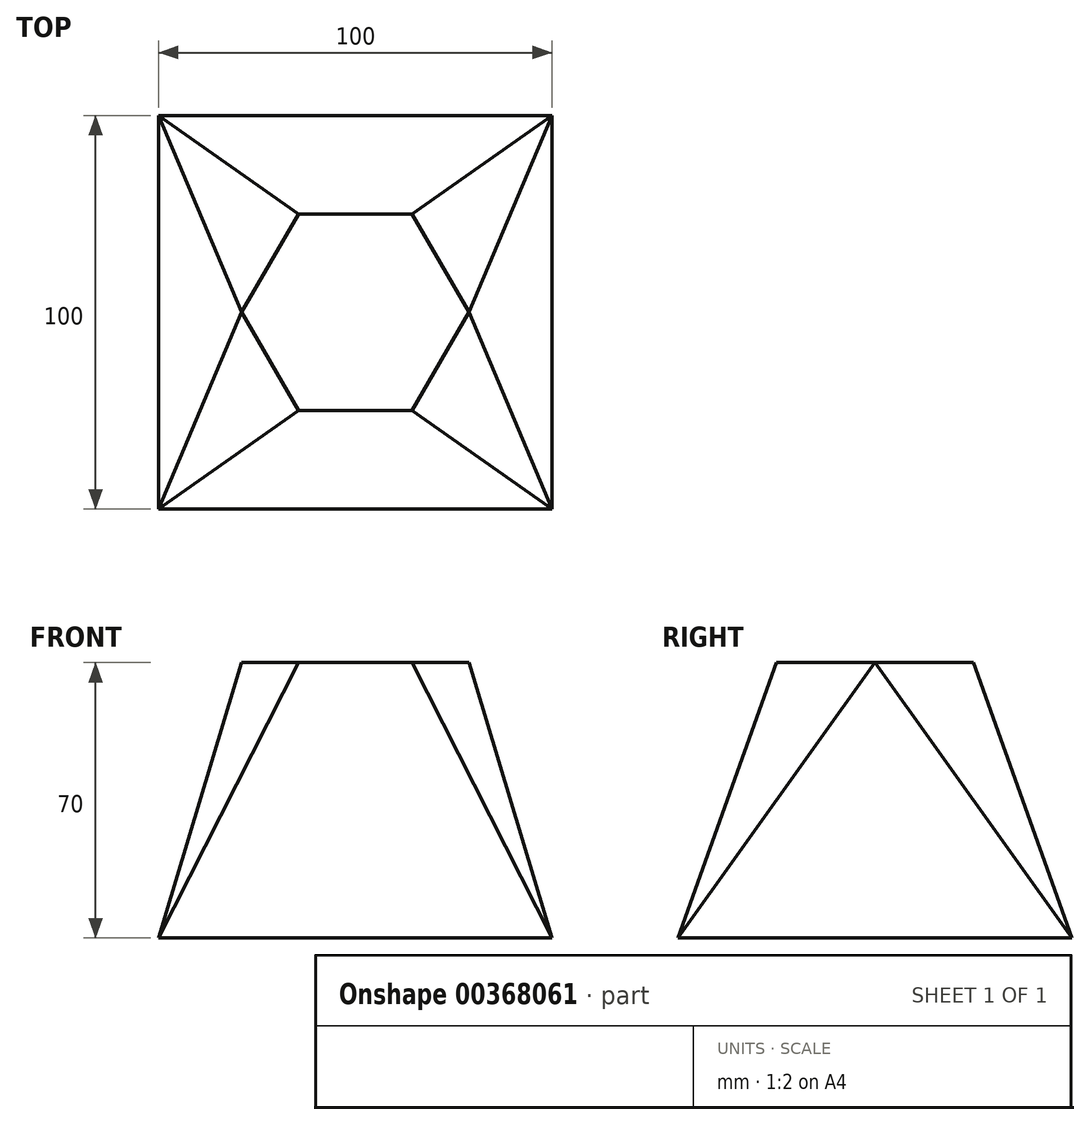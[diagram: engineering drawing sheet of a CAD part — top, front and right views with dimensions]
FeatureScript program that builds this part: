
annotation { "Feature Type Name" : "Feature", "Feature Type Description" : "" }
export const myFeature = defineFeature(function(context is Context, id is Id, definition is map)
    precondition{}
    {
        {
            var Q0;
            Q0=qCreatedBy(makeId("Top.planeOp"),FACE);
            var sketch = newSketch(context, id + "F0", { "sketchPlane" : qUnion([Q0])});
            skLineSegment(sketch, "E0.bottom", {"start": v(50, -50) * mm, "end": v(-50, -50) * mm});
            skLineSegment(sketch, "E0.top", {"start": v(50, 50) * mm, "end": v(-50, 50) * mm});
            skLineSegment(sketch, "E0.left", {"start": v(50, -50) * mm, "end": v(50, 50) * mm});
            skLineSegment(sketch, "E0.right", {"start": v(-50, -50) * mm, "end": v(-50, 50) * mm});
            skPoint(sketch, "E0.middle", {"position": v(0, 0) * mm});
            skSolve(sketch);
        }
        {
            var Q0;
            Q0=qCreatedBy(makeId("Top.planeOp"),FACE);
            cPlane(context, id + "F1", {"entities" : qUnion([Q0]), "cplaneType" : CPlaneType.OFFSET, "offset" : 70 * mm, "width" : 150 * mm, "height" : 150 * mm});
        }
        {
            var Q0;
            Q0=qCreatedBy(id+"F1.planeOp",FACE);
            var sketch = newSketch(context, id + "F2", { "sketchPlane" : qUnion([Q0])});
            skCircle(sketch, "E1.cCircle", {"center": v(0, 0) * mm, "radius": 25 * mm, "construction": true});
            skLineSegment(sketch, "E1.0", {"start": v(-14.43, 25) * mm, "end": v(14.43, 25) * mm});
            skLineSegment(sketch, "E1.1", {"start": v(14.43, 25) * mm, "end": v(28.87, 0) * mm});
            skLineSegment(sketch, "E1.2", {"start": v(28.87, 0) * mm, "end": v(14.43, -25) * mm});
            skLineSegment(sketch, "E1.3", {"start": v(14.43, -25) * mm, "end": v(-14.43, -25) * mm});
            skLineSegment(sketch, "E1.4", {"start": v(-14.43, -25) * mm, "end": v(-28.87, 0) * mm});
            skLineSegment(sketch, "E1.5", {"start": v(-28.87, 0) * mm, "end": v(-14.43, 25) * mm});
            skPoint(sketch, "E1.0.midPoint", {"position": v(0, 25) * mm});
            skLineSegment(sketch, "E2", {"start": v(-14.43, 25) * mm, "end": v(-14.43, -25) * mm});
            skLineSegment(sketch, "E3", {"start": v(14.43, 25) * mm, "end": v(14.43, -25) * mm});
            skSolve(sketch);
        }
        {
            var Q0;
            Q0=makeQuery(id+"F2.imprint","IMPRINT",FACE,{"disambiguationData":[TD([[makeQuery(id+"F2.imprint","IMPRINT",EDGE,{"derivedFrom":sQuery(id+"F2.wireOp",EDGE,"E1.0")}),-1.0]])]});
            var Q1;
            Q1=makeQuery(id+"F0.imprint","IMPRINT",FACE,{"disambiguationData":[TD([[makeQuery(id+"F0.imprint","IMPRINT",EDGE,{"derivedFrom":sQuery(id+"F0.wireOp",EDGE,"E0.bottom")}),-1.0]])]});
            loft(context, id + "F3", {"sheetProfilesArray" : [{ "sheetProfileEntities" : qUnion([Q0]) }, { "sheetProfileEntities" : qUnion([Q1]) }]});
        }
        {
            var Q1;
            Q1=makeQuery(id+"F2.imprint","IMPRINT",FACE,{"disambiguationData":[TD([[makeQuery(id+"F2.imprint","IMPRINT",EDGE,{"derivedFrom":sQuery(id+"F2.wireOp",EDGE,"E1.4")}),-1.0]])]});
            var Q2;
            Q2=makeQuery(id+"F3.opLoft","MID_CAP_VERTEX",VERTEX,{"disambiguationData":[OSD([sQuery(id+"F0.wireOp",EDGE,"E0.bottom"),sQuery(id+"F0.wireOp",EDGE,"E0.right")])],"capPos":1.0});
            loft(context, id + "F4", {"operationType" : NewBodyOperationType.ADD, "sheetProfilesArray" : [{ "sheetProfileEntities" : qUnion([Q1]) }, { "sheetProfileEntities" : qUnion([Q2]) }]});
        }
        {
            var Q1;
            Q1=makeQuery(id+"F2.imprint","IMPRINT",FACE,{"disambiguationData":[TD([[makeQuery(id+"F2.imprint","IMPRINT",EDGE,{"derivedFrom":sQuery(id+"F2.wireOp",EDGE,"E1.4")}),-1.0]])]});
            var Q2;
            Q2=makeQuery(id+"F3.opLoft","MID_CAP_VERTEX",VERTEX,{"disambiguationData":[OSD([sQuery(id+"F0.wireOp",EDGE,"E0.top"),sQuery(id+"F0.wireOp",EDGE,"E0.right")])],"capPos":1.0});
            loft(context, id + "F5", {"operationType" : NewBodyOperationType.ADD, "sheetProfilesArray" : [{ "sheetProfileEntities" : qUnion([Q1]) }, { "sheetProfileEntities" : qUnion([Q2]) }]});
        }
        {
            var Q1;
            Q1=makeQuery(id+"F5.opLoft","SWEPT_FACE",FACE,{"disambiguationData":[OSD([sQuery(id+"F2.wireOp",EDGE,"E1.3"),sQuery(id+"F2.wireOp",EDGE,"E1.4"),sQuery(id+"F2.wireOp",EDGE,"E1.5"),sQuery(id+"F2.wireOp",EDGE,"E2")])]});
            var Q2;
            Q2=makeQuery(id+"F4.opLoft","SWEPT_FACE",FACE,{"disambiguationData":[OSD([sQuery(id+"F2.wireOp",EDGE,"E1.0"),sQuery(id+"F2.wireOp",EDGE,"E1.4"),sQuery(id+"F2.wireOp",EDGE,"E1.5"),sQuery(id+"F2.wireOp",EDGE,"E2")])]});
            var Q3;
            {var subQ0=sQuery(id+"F0.wireOp",EDGE,"E0.right");var subQ1=sQuery(id+"F0.wireOp",EDGE,"E0.top");Q3=makeQuery(id+"F5.boolean.opBoolean","MERGE",VERTEX,{"derivedFrom":[makeQuery(id+"F3.opLoft","MID_CAP_VERTEX",VERTEX,{"disambiguationData":[OSD([subQ1,subQ0])],"capPos":1.0}),makeQuery(id+"F5.opLoft","SWEPT_VERTEX",VERTEX,{"disambiguationData":[OSD([subQ1,subQ0,sQuery(id+"F2.wireOp",EDGE,"E1.3"),sQuery(id+"F2.wireOp",EDGE,"E1.4"),sQuery(id+"F2.wireOp",EDGE,"E2")])]})]});}
            var Q4;
            {var subQ0=sQuery(id+"F0.wireOp",EDGE,"E0.right");var subQ1=sQuery(id+"F0.wireOp",EDGE,"E0.bottom");Q4=makeQuery(id+"F4.boolean.opBoolean","MERGE",VERTEX,{"derivedFrom":[makeQuery(id+"F3.opLoft","MID_CAP_VERTEX",VERTEX,{"disambiguationData":[OSD([subQ1,subQ0])],"capPos":1.0}),makeQuery(id+"F4.opLoft","SWEPT_VERTEX",VERTEX,{"disambiguationData":[OSD([subQ1,subQ0,sQuery(id+"F2.wireOp",EDGE,"E1.3"),sQuery(id+"F2.wireOp",EDGE,"E1.4"),sQuery(id+"F2.wireOp",EDGE,"E2")])]})]});}
            loft(context, id + "F6", {"operationType" : NewBodyOperationType.ADD, "sheetProfilesArray" : [{ "sheetProfileEntities" : qUnion([Q1]) }, { "sheetProfileEntities" : qUnion([Q2]) }], "matchConnections" : true, "connections" : [{ "connectionEntities" : qUnion([Q3, Q4]), "connectionEdgeQueries" : qUnion([]), "connectionEdgeParameters" : [] }]});
        }
        {
            var Q1;
            Q1=makeQuery(id+"F2.imprint","IMPRINT",FACE,{"disambiguationData":[TD([[makeQuery(id+"F2.imprint","IMPRINT",EDGE,{"derivedFrom":sQuery(id+"F2.wireOp",EDGE,"E1.1")}),-1.0]])]});
            var Q2;
            Q2=makeQuery(id+"F3.opLoft","MID_CAP_VERTEX",VERTEX,{"disambiguationData":[OSD([sQuery(id+"F0.wireOp",EDGE,"E0.top"),sQuery(id+"F0.wireOp",EDGE,"E0.left")])],"capPos":1.0});
            loft(context, id + "F7", {"operationType" : NewBodyOperationType.ADD, "sheetProfilesArray" : [{ "sheetProfileEntities" : qUnion([Q1]) }, { "sheetProfileEntities" : qUnion([Q2]) }]});
        }
        {
            var Q1;
            Q1=makeQuery(id+"F3.opLoft","MID_CAP_VERTEX",VERTEX,{"disambiguationData":[OSD([sQuery(id+"F0.wireOp",EDGE,"E0.bottom"),sQuery(id+"F0.wireOp",EDGE,"E0.left")])],"capPos":1.0});
            var Q2;
            Q2=makeQuery(id+"F2.imprint","IMPRINT",FACE,{"disambiguationData":[TD([[makeQuery(id+"F2.imprint","IMPRINT",EDGE,{"derivedFrom":sQuery(id+"F2.wireOp",EDGE,"E1.1")}),-1.0]])]});
            loft(context, id + "F8", {"operationType" : NewBodyOperationType.ADD, "sheetProfilesArray" : [{ "sheetProfileEntities" : qUnion([Q1]) }, { "sheetProfileEntities" : qUnion([Q2]) }]});
        }
        {
            var Q1;
            Q1=makeQuery(id+"F8.opLoft","SWEPT_FACE",FACE,{"disambiguationData":[OSD([sQuery(id+"F2.wireOp",EDGE,"E1.0"),sQuery(id+"F2.wireOp",EDGE,"E1.1"),sQuery(id+"F2.wireOp",EDGE,"E1.2"),sQuery(id+"F2.wireOp",EDGE,"E3")])]});
            var Q2;
            Q2=makeQuery(id+"F7.opLoft","SWEPT_FACE",FACE,{"disambiguationData":[OSD([sQuery(id+"F2.wireOp",EDGE,"E1.1"),sQuery(id+"F2.wireOp",EDGE,"E1.2"),sQuery(id+"F2.wireOp",EDGE,"E1.3"),sQuery(id+"F2.wireOp",EDGE,"E3")])]});
            var Q3;
            {var subQ0=sQuery(id+"F0.wireOp",EDGE,"E0.left");var subQ1=sQuery(id+"F0.wireOp",EDGE,"E0.top");Q3=makeQuery(id+"F7.boolean.opBoolean","MERGE",VERTEX,{"derivedFrom":[makeQuery(id+"F3.opLoft","MID_CAP_VERTEX",VERTEX,{"disambiguationData":[OSD([subQ1,subQ0])],"capPos":1.0}),makeQuery(id+"F7.opLoft","SWEPT_VERTEX",VERTEX,{"disambiguationData":[OSD([subQ1,subQ0,sQuery(id+"F2.wireOp",EDGE,"E1.1"),sQuery(id+"F2.wireOp",EDGE,"E1.2")])]})]});}
            var Q4;
            {var subQ0=sQuery(id+"F0.wireOp",EDGE,"E0.left");var subQ1=sQuery(id+"F0.wireOp",EDGE,"E0.bottom");Q4=makeQuery(id+"F8.boolean.opBoolean","MERGE",VERTEX,{"derivedFrom":[makeQuery(id+"F3.opLoft","MID_CAP_VERTEX",VERTEX,{"disambiguationData":[OSD([subQ1,subQ0])],"capPos":1.0}),makeQuery(id+"F8.opLoft","SWEPT_VERTEX",VERTEX,{"disambiguationData":[OSD([subQ1,subQ0,sQuery(id+"F2.wireOp",EDGE,"E1.1"),sQuery(id+"F2.wireOp",EDGE,"E1.2")])]})]});}
            loft(context, id + "F9", {"operationType" : NewBodyOperationType.ADD, "sheetProfilesArray" : [{ "sheetProfileEntities" : qUnion([Q1]) }, { "sheetProfileEntities" : qUnion([Q2]) }], "matchConnections" : true, "connections" : [{ "connectionEntities" : qUnion([Q3, Q4]), "connectionEdgeQueries" : qUnion([]), "connectionEdgeParameters" : [] }]});
        }
    });
